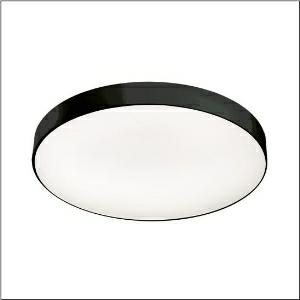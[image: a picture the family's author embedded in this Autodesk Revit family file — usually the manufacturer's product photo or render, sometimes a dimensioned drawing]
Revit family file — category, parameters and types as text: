
# Revit family: round_21_l_51mr38nd0321b
name_source: partatom
category: Lighting Fixtures
units: mm (PartAtom-declared; Revit-internal decimal feet)

## family parameters
Cut with Voids When Loaded = No
Host = Face
Light Source = No
Part Type = Normal
Room Calculation Point = No
Round Connector Dimension = Use Diameter
Shared = No

## types (1)
- Round 21 L (1 x LED, 11740 lm, 88.2 W, 3000K)
    Apparent Load = 88 VA
    CIE Flux Codes = 66 90 98 71 100
    Color Rendering = 80
    Color Temperature = 3000K
    Default Elevation = 1800 mm
    Description = Round 21 L, wall and ceiling luminaire, primary optical cover: micro prismatic cover, of PMMA, transparent, CAT 2 (L<= 3000cd/m²), light emission: direct/indirect distribution, primary light characteristic: symmetric, installation type: suspended mounting, surface-mounted, LED, rated luminous flux: 11.740lm, luminous efficacy: 133lm/W, light colour: 830, colour temperature: 3000K, control gear: DALI 2, with terminal, 5-pole, mains connection: 230V, AC, 50/60Hz, rated input power: 88.2W, housing, of aluminium, coated, black, diameter: 850mm, height: 62mm, protection rating (complete): IP40, insulation class (complete): insulation class I (protective earthing), certification: CE, impact resistance: IK04, permissible operating ambient temperature: -10..+35°C, packaging unit: 1 piece
    Height = 87 mm
    Lamp = 1 x LED
    Lamp Light Flux = 11740 lm
    Lamp Power = 88.2 W
    Lamp count = 1
    Length = 850 mm
    Luminous efficacy = 133 lm/W
    Manufacturer = Siteco
    ModVariant = No
    Model = 51MR38ND0321B
    Mounting Place = Ceiling
    Mounting Type = Surface mounted
    Number of Poles = 1
    OnlyDefault = Yes
    Power Factor = 1
    Product Name = Round 21 L
    Product group = wall and ceiling luminaire
    ProductGroupID = 304
    Protection Class = Protection class I
    Protection Degree = IP 40
    RLX_Detail_Level = 1
    RLX_Emergency_Light_Flux = 0 lm
    RLX_Emergency_Type = 0
    RLX_Emergency_Type_DB = No
    RlxData = <blob elided: 28737 chars, md5=cee69943>
    Socket = socket
    Standby Power = 0 W
    System Light Flux = 11740 lm
    System Power = 88 W
    Type Comments = Product without accessories
    Type Image = l_1258326.jpg
    URL = http://relux.com
    VarID = ---
    Voltage = 0 V
    Weight = 0.00 kg
    Width = 0 mm  [stored 0 ft]

note: [stored X ft] marks values corroborated as IEEE doubles in the binary element streams (Revit-internal decimal feet)

## geometry (parser evidence)
native form markers: Blend x4, Sweep x12
no freeform markers — native parametric forms only
